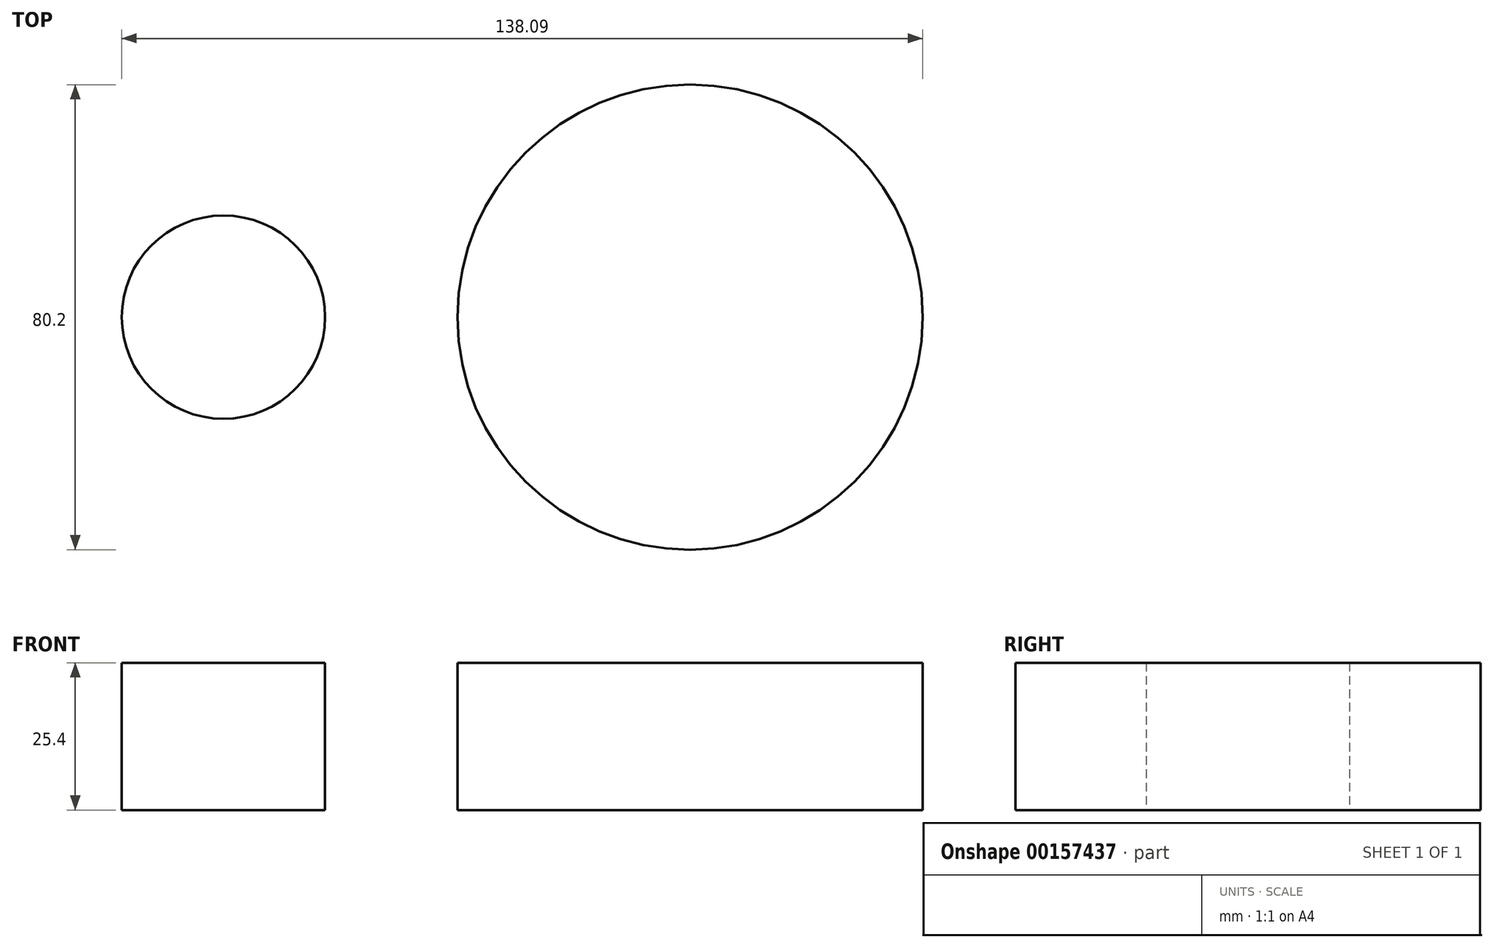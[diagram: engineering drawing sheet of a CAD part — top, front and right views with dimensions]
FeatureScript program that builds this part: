
annotation { "Feature Type Name" : "Feature", "Feature Type Description" : "" }
export const myFeature = defineFeature(function(context is Context, id is Id, definition is map)
    precondition{}
    {
        {
            var Q0;
            Q0=qCreatedBy(makeId("Top.planeOp"),FACE);
            var sketch = newSketch(context, id + "F0", { "sketchPlane" : qUnion([Q0])});
            skCircle(sketch, "E0", {"center": v(-57.51, 0) * mm, "radius": 17.53 * mm});
            skCircle(sketch, "E1", {"center": v(22.95, 0) * mm, "radius": 40.1 * mm});
            skLineSegment(sketch, "E2", {"start": v(-56.94, 17.52) * mm, "end": v(7.47, 37) * mm});
            skLineSegment(sketch, "E3", {"start": v(-55.21, -17.38) * mm, "end": v(10.87, -38.24) * mm});
            skSolve(sketch);
        }
        {
            var Q0;
            {var subQ0=sQuery(id+"F0.wireOp",EDGE,"E0");var subQ1=makeQuery(id+"F0.imprint","INTERSECT",VERTEX,{"derivedFrom":[subQ0,sQuery(id+"F0.wireOp",EDGE,"E2")]});Q0=makeQuery(id+"F0.imprint","IMPRINT",FACE,{"disambiguationData":[TD([[makeQuery(id+"F0.imprint","IMPRINT",EDGE,{"disambiguationData":[TD([[subQ1,-1.0]])],"derivedFrom":subQ0}),1.0]])]});}
            var Q1;
            {var subQ0=sQuery(id+"F0.wireOp",EDGE,"E1");var subQ1=makeQuery(id+"F0.imprint","INTERSECT",VERTEX,{"derivedFrom":[subQ0,sQuery(id+"F0.wireOp",EDGE,"E2")]});Q1=makeQuery(id+"F0.imprint","IMPRINT",FACE,{"disambiguationData":[TD([[makeQuery(id+"F0.imprint","IMPRINT",EDGE,{"disambiguationData":[TD([[subQ1,-1.0]])],"derivedFrom":subQ0}),1.0]])]});}
            extrude(context, id + "F1", {"entities" : qUnion([Q0, Q1]), "depth" : 25.4 * mm});
        }
    });
